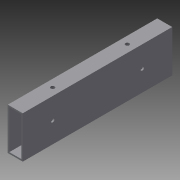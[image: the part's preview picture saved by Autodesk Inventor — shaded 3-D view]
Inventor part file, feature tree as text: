
AUTODESK INVENTOR PART (.ipt)
format: ipt  version: 2015 (Build 190159000, 159)  size: 104,448 bytes
history: native  units: in
note: dims shown in document units (in); Inventor stores cm internally (conversion verified against a paired STEP export)
features: sketch x3, hole x2, extrude x1, projected_geometry x1
ambient origin geometry x8: Origin, YZ Plane, XZ Plane, XY Plane, X Axis, Y Axis, Z Axis, Center Point
bodies: Solid1 (feature_tree)
feature tree (7):
  extrude  "Extrusion1"  Depth=0.5in
  hole  "Hole1"  [1 undecoded]
  hole  "Hole3"  [1 undecoded]
  sketch  "Sketch1"  dims[d0=1.4in d1=0.5in]
  sketch  "Sketch2"  dims[d2=0.05in d3=5.0in d4=0.0in]
  sketch  "Sketch4"  dims[d5=0.7in d6=1.0in d7=1.0in d11=0.1285in d12=0.75in d13=0.375in d14=0.25in d15=0.5635in d16=1.0in d17=0.8108in d27=0.25in d28=1.25in d29=1.25in d30=0.128in d31=0.75in d32=0.375in d33=0.25in d34=0.5635in d35=1.0in d36=0.8108in]
  projected_geometry  "Projected Loop1"
note: 2 required parameter values undecoded (feature->parameter linkage not recoverable at this tier; creation-order binding heuristic only, values carry confidence <= 0.55)
